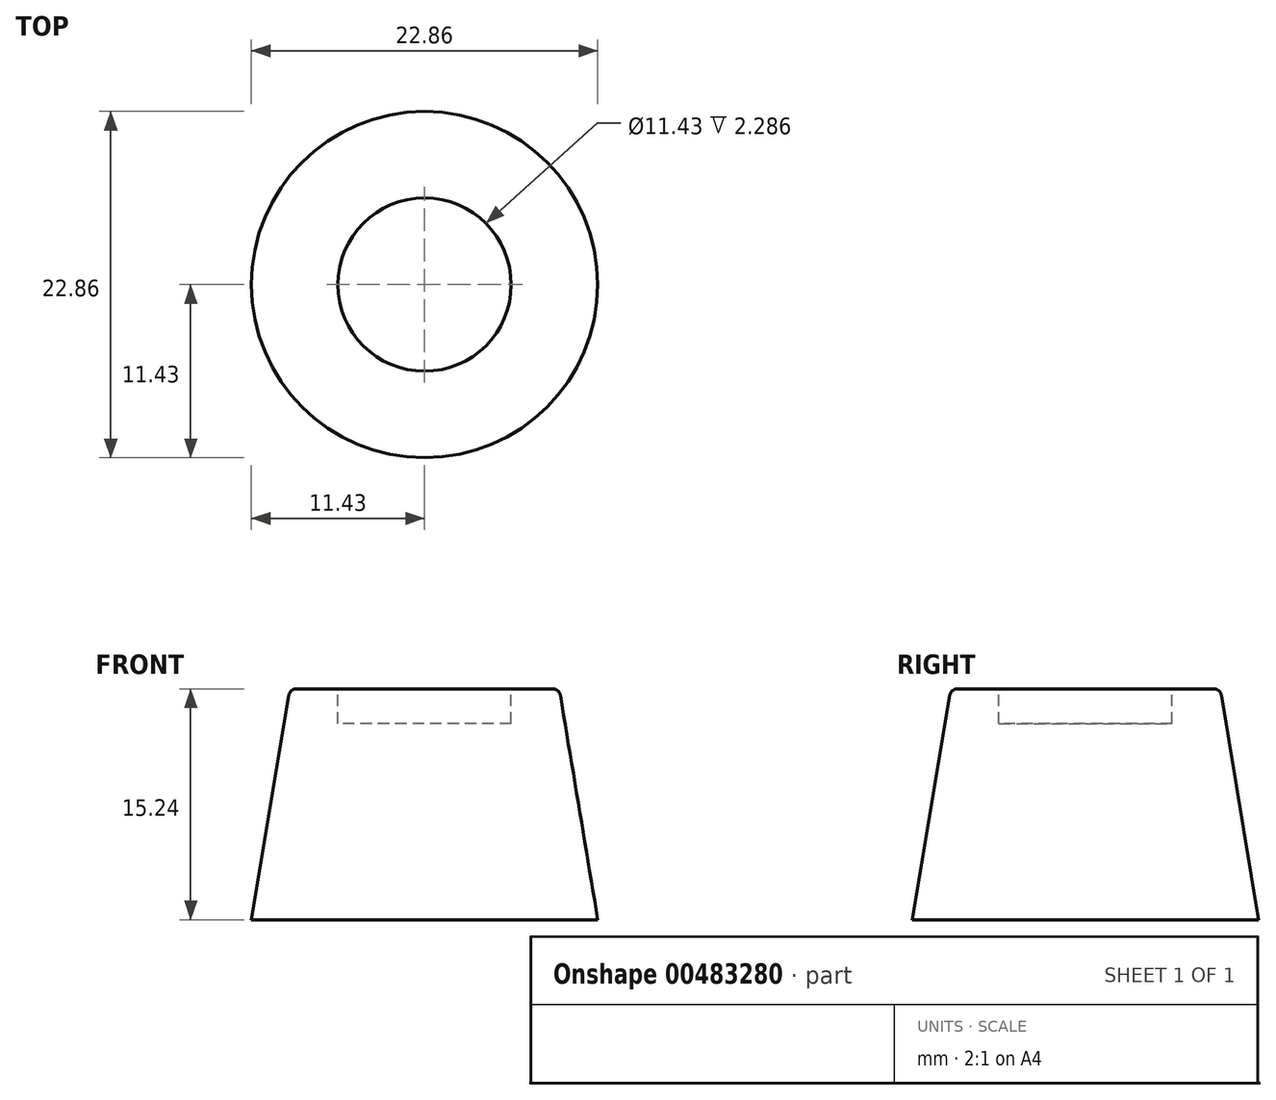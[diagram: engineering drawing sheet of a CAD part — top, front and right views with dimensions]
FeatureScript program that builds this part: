
annotation { "Feature Type Name" : "Feature", "Feature Type Description" : "" }
export const myFeature = defineFeature(function(context is Context, id is Id, definition is map)
    precondition{}
    {
        {
            var Q0;
            Q0=qCreatedBy(makeId("Top.planeOp"),FACE);
            var sketch = newSketch(context, id + "F0", { "sketchPlane" : qUnion([Q0])});
            skCircle(sketch, "E0", {"center": v(0, 0) * mm, "radius": 11.43 * mm});
            skSolve(sketch);
        }
        {
            var Q0;
            Q0=qCreatedBy(makeId("Top.planeOp"),FACE);
            cPlane(context, id + "F1", {"entities" : qUnion([Q0]), "cplaneType" : CPlaneType.OFFSET, "offset" : 15.24 * mm, "width" : 152.4 * mm, "height" : 152.4 * mm});
        }
        {
            var Q0;
            Q0=qCreatedBy(id+"F1.planeOp",FACE);
            var sketch = newSketch(context, id + "F2", { "sketchPlane" : qUnion([Q0])});
            skPoint(sketch, "E1.0", {"position": v(0, 0) * mm});
            skCircle(sketch, "E2", {"center": v(0, 0) * mm, "radius": 8.9 * mm});
            skSolve(sketch);
        }
        {
            var Q0;
            Q0=makeQuery(id+"F0.imprint","IMPRINT",FACE,{"disambiguationData":[TD([[makeQuery(id+"F0.imprint","IMPRINT",EDGE,{"derivedFrom":sQuery(id+"F0.wireOp",EDGE,"E0")}),1.0]])]});
            var Q1;
            Q1=makeQuery(id+"F2.imprint","IMPRINT",FACE,{"disambiguationData":[TD([[makeQuery(id+"F2.imprint","IMPRINT",EDGE,{"derivedFrom":sQuery(id+"F2.wireOp",EDGE,"E2")}),1.0]])]});
            loft(context, id + "F3", {"sheetProfilesArray" : [{ "sheetProfileEntities" : qUnion([Q0]) }, { "sheetProfileEntities" : qUnion([Q1]) }]});
        }
        {
            var Q0;
            Q0=makeQuery(id+"F3.opLoft","CAP_FACE",FACE,{"disambiguationData":[OSD([makeQuery(id+"F2.imprint","IMPRINT",FACE,{"disambiguationData":[TD([[makeQuery(id+"F2.imprint","IMPRINT",EDGE,{"derivedFrom":sQuery(id+"F2.wireOp",EDGE,"E2")}),1.0]])]})])],"isStart":true});
            var sketch = newSketch(context, id + "F4", { "sketchPlane" : qUnion([Q0])});
            skCircle(sketch, "E3", {"center": v(0, 0) * mm, "radius": 5.72 * mm});
            skSolve(sketch);
        }
        {
            var Q0;
            Q0=makeQuery(id+"F4.imprint","IMPRINT",FACE,{"disambiguationData":[TD([[makeQuery(id+"F4.imprint","IMPRINT",EDGE,{"derivedFrom":sQuery(id+"F4.wireOp",EDGE,"E3")}),1.0]])]});
            extrude(context, id + "F5", {"entities" : qUnion([Q0]), "operationType" : NewBodyOperationType.REMOVE, "oppositeDirection" : true, "depth" : 2.3 * mm});
        }
        {
            var Q0;
            Q0=makeQuery(id+"F5.boolean.opBoolean","COPY",EDGE,{"derivedFrom":makeQuery(id+"F5.opExtrude","CAP_EDGE",EDGE,{"disambiguationData":[OSD([sQuery(id+"F4.wireOp",EDGE,"E3")])],"isStart":true})});
            var Q1;
            Q1=makeQuery(id+"F3.opLoft","MID_CAP_EDGE",EDGE,{"disambiguationData":[OSD([sQuery(id+"F0.wireOp",EDGE,"E0"),sQuery(id+"F2.wireOp",EDGE,"E2")])],"capPos":1.0});
            fillet(context, id + "F6", {"entities" : qUnion([Q0, Q1]), "radius" : 0.5 * mm, "tangentPropagation" : true, "allowEdgeOverflow" : false});
        }
    });
